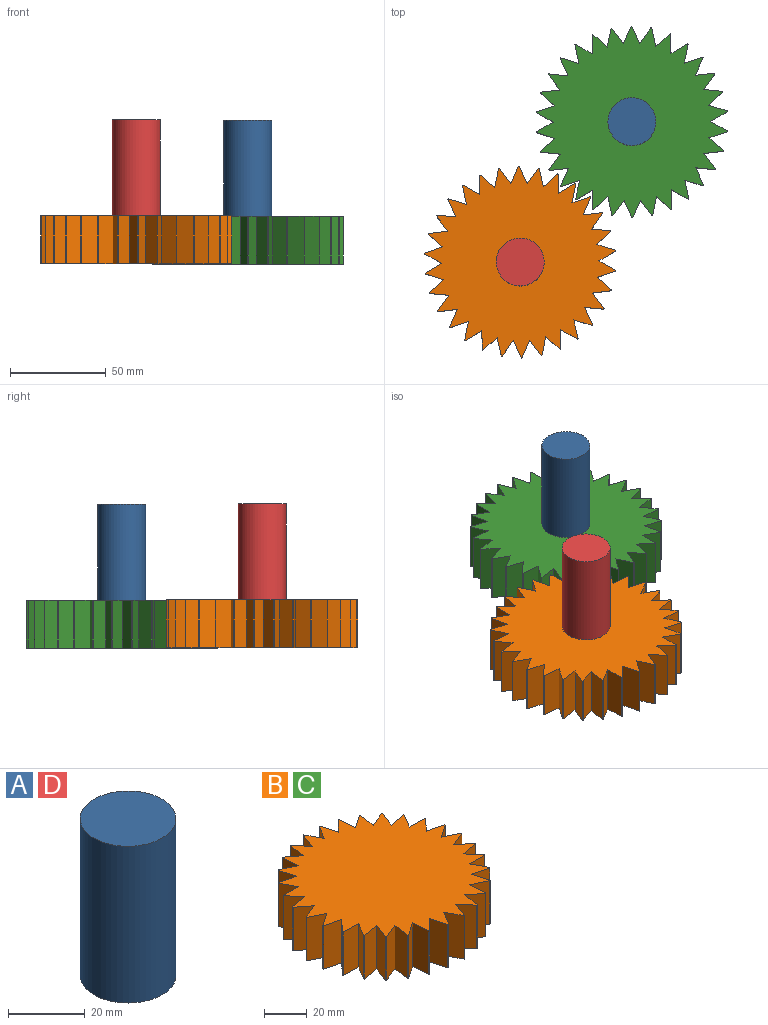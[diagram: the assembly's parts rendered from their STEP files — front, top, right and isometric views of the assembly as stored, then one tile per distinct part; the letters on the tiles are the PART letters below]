
ASSEMBLY  parts=4 mates=2
PART A: 3 faces, bbox 25x25x50 mm
  f0: cylinder r=12.5mm len=50mm, axis (0,0,-1), area 3927mm2, adj f1,f2
  f1: plane 25x25mm, normal (0,0,1), area 490.9mm2, adj f0
  f2: plane 25x25mm, normal (0,0,-1), area 490.9mm2, adj f0
PART B: 92 faces, bbox 100x99.8x25 mm
  f0: cylinder r=50mm len=25mm, axis (0,0,-1), area 11.4mm2, adj f30,f31,f59,f90
  f1: cylinder r=50mm len=25mm, axis (0,0,-1), area 11.4mm2, adj f30,f31,f77,f88
  f2: cylinder r=50mm len=25mm, axis (0,0,-1), area 11.4mm2, adj f30,f31,f55,f86
  f3: cylinder r=50mm len=25mm, axis (0,0,-1), area 11.4mm2, adj f30,f31,f49,f84
  f4: cylinder r=50mm len=25mm, axis (0,0,-1), area 11.4mm2, adj f30,f31,f82,f85
  f5: cylinder r=50mm len=25mm, axis (0,0,-1), area 11.4mm2, adj f30,f31,f63,f80
  f6: cylinder r=50mm len=25mm, axis (0,0,-1), area 11.4mm2, adj f30,f31,f33,f78
  f7: cylinder r=50mm len=25mm, axis (0,0,-1), area 11.4mm2, adj f30,f31,f71,f76
  f8: cylinder r=50mm len=25mm, axis (0,0,-1), area 11.4mm2, adj f30,f31,f69,f74
  f9: cylinder r=50mm len=25mm, axis (0,0,-1), area 11.4mm2, adj f30,f31,f39,f72
  f10: cylinder r=50mm len=25mm, axis (0,0,-1), area 11.4mm2, adj f30,f31,f67,f70
  f11: cylinder r=50mm len=25mm, axis (0,0,-1), area 11.4mm2, adj f30,f31,f68,f91
  f12: cylinder r=50mm len=25mm, axis (0,0,-1), area 11.4mm2, adj f30,f31,f66,f75
  f13: cylinder r=50mm len=25mm, axis (0,0,-1), area 11.4mm2, adj f30,f31,f53,f64
  f14: cylinder r=50mm len=25mm, axis (0,0,-1), area 11.4mm2, adj f30,f31,f62,f65
  f15: cylinder r=50mm len=25mm, axis (0,0,-1), area 11.4mm2, adj f30,f31,f60,f81
  f16: cylinder r=50mm len=25mm, axis (0,0,-1), area 11.4mm2, adj f30,f31,f58,f73
  f17: cylinder r=50mm len=25mm, axis (0,0,-1), area 11.4mm2, adj f30,f31,f56,f83
  f18: cylinder r=50mm len=25mm, axis (0,0,-1), area 11.4mm2, adj f30,f31,f47,f54
  f19: cylinder r=50mm len=25mm, axis (0,0,-1), area 11.4mm2, adj f30,f31,f35,f52
  f20: cylinder r=50mm len=25mm, axis (0,0,-1), area 11.4mm2, adj f30,f31,f50,f79
  f21: cylinder r=50mm len=25mm, axis (0,0,-1), area 11.4mm2, adj f30,f31,f48,f51
  f22: cylinder r=50mm len=25mm, axis (0,0,-1), area 11.4mm2, adj f30,f31,f46,f89
  f23: cylinder r=50mm len=25mm, axis (0,0,-1), area 11.4mm2, adj f30,f31,f37,f44
  f24: cylinder r=50mm len=25mm, axis (0,0,-1), area 11.4mm2, adj f30,f31,f42,f87
  f25: cylinder r=50mm len=25mm, axis (0,0,-1), area 11.4mm2, adj f30,f31,f40,f57
  f26: cylinder r=50mm len=25mm, axis (0,0,-1), area 11.4mm2, adj f30,f31,f38,f45
  f27: cylinder r=50mm len=25mm, axis (0,0,-1), area 11.4mm2, adj f30,f31,f36,f61
  f28: cylinder r=50mm len=25mm, axis (0,0,-1), area 11.4mm2, adj f30,f31,f34,f41
  f29: cylinder r=50mm len=25mm, axis (0,0,-1), area 11.4mm2, adj f30,f31,f32,f43
  f30: plane 99.96x99.77mm, normal (0,0,1), area 6504.8mm2, adj f0,f1,f2,f3,f4,f5,f6,f7
  f31: plane 99.96x99.77mm, normal (0,0,-1), area 6504.8mm2, adj f0,f1,f2,f3,f4,f5,f6,f7
  f32: plane 25x9mm, normal (0.44,0.9,0), area 250mm2, adj f29,f30,f31,f33
  f33: plane 25x9.97mm, normal (-1,-0.07,0), area 250mm2, adj f6,f30,f31,f32
  f34: plane 25x8.49mm, normal (0.85,-0.53,0), area 250mm2, adj f28,f30,f31,f35
  f35: plane 25x9.99mm, normal (0.03,1,0), area 250mm2, adj f19,f30,f31,f34
  f36: plane 25x9.71mm, normal (-0.24,-0.97,0), area 250mm2, adj f27,f30,f31,f37
  f37: plane 25x9.61mm, normal (0.96,0.28,0), area 250mm2, adj f23,f30,f31,f36
  f38: plane 25x7.89mm, normal (-0.61,-0.79,0), area 250mm2, adj f26,f30,f31,f39
  f39: plane 25x9.91mm, normal (0.99,-0.14,0), area 250mm2, adj f9,f30,f31,f38
  f40: plane 25x9.4mm, normal (0.94,-0.34,0), area 250mm2, adj f25,f30,f31,f41
  f41: plane 25x9.84mm, normal (-0.18,0.98,0), area 250mm2, adj f28,f30,f31,f40
  f42: plane 25x9.71mm, normal (0.24,0.97,0), area 250mm2, adj f24,f30,f31,f43
  f43: plane 25x9.61mm, normal (-0.96,-0.28,0), area 250mm2, adj f29,f30,f31,f42
  f44: plane 25x9mm, normal (-0.44,-0.9,0), area 250mm2, adj f23,f30,f31,f45
  f45: plane 25x9.97mm, normal (1,0.07,0), area 250mm2, adj f26,f30,f31,f44
  f46: plane 25x9.26mm, normal (-0.38,0.93,0), area 250mm2, adj f22,f30,f31,f47
  f47: plane 25x7.89mm, normal (-0.61,-0.79,0), area 250mm2, adj f18,f30,f31,f46
  f48: plane 25x8.82mm, normal (0.88,0.47,0), area 250mm2, adj f21,f30,f31,f49
  f49: plane 25x8.49mm, normal (-0.85,0.53,0), area 250mm2, adj f3,f30,f31,f48
  f50: plane 25x7.65mm, normal (0.76,0.64,0), area 250mm2, adj f20,f30,f31,f51
  f51: plane 25x9.4mm, normal (-0.94,0.34,0), area 250mm2, adj f21,f30,f31,f50
  f52: plane 25x7.21mm, normal (0.72,-0.69,0), area 250mm2, adj f19,f30,f31,f53
  f53: plane 25x9.71mm, normal (0.24,0.97,0), area 250mm2, adj f13,f30,f31,f52
  f54: plane 25x9.84mm, normal (-0.18,0.98,0), area 250mm2, adj f18,f30,f31,f55
  f55: plane 25x7.65mm, normal (-0.76,-0.64,0), area 250mm2, adj f2,f30,f31,f54
  f56: plane 25x9.91mm, normal (0.99,-0.14,0), area 250mm2, adj f17,f30,f31,f57
  f57: plane 25x9.26mm, normal (-0.38,0.93,0), area 250mm2, adj f25,f30,f31,f56
  f58: plane 25x8.82mm, normal (-0.88,-0.47,0), area 250mm2, adj f16,f30,f31,f59
  f59: plane 25x8.49mm, normal (0.85,-0.53,0), area 250mm2, adj f0,f30,f31,f58
  f60: plane 25x9.99mm, normal (-0.03,-1,0), area 250mm2, adj f15,f30,f31,f61
  f61: plane 25x8.82mm, normal (0.88,0.47,0), area 250mm2, adj f27,f30,f31,f60
  f62: plane 25x9.26mm, normal (0.38,-0.93,0), area 250mm2, adj f14,f30,f31,f63
  f63: plane 25x7.89mm, normal (0.61,0.79,0), area 250mm2, adj f5,f30,f31,f62
  f64: plane 25x8.28mm, normal (0.56,-0.83,0), area 250mm2, adj f13,f30,f31,f65
  f65: plane 25x9mm, normal (0.44,0.9,0), area 250mm2, adj f14,f30,f31,f64
  f66: plane 25x9.4mm, normal (-0.94,0.34,0), area 250mm2, adj f12,f30,f31,f67
  f67: plane 25x9.84mm, normal (0.18,-0.98,0), area 250mm2, adj f10,f30,f31,f66
  f68: plane 25x9.97mm, normal (-1,-0.07,0), area 250mm2, adj f11,f30,f31,f69
  f69: plane 25x8.28mm, normal (0.56,-0.83,0), area 250mm2, adj f8,f30,f31,f68
  f70: plane 25x8.49mm, normal (-0.85,0.53,0), area 250mm2, adj f10,f30,f31,f71
  f71: plane 25x9.99mm, normal (-0.03,-1,0), area 250mm2, adj f7,f30,f31,f70
  f72: plane 25x7.65mm, normal (-0.76,-0.64,0), area 250mm2, adj f9,f30,f31,f73
  f73: plane 25x9.4mm, normal (0.94,-0.34,0), area 250mm2, adj f16,f30,f31,f72
  f74: plane 25x9.91mm, normal (-0.99,0.14,0), area 250mm2, adj f8,f30,f31,f75
  f75: plane 25x9.26mm, normal (0.38,-0.93,0), area 250mm2, adj f12,f30,f31,f74
  f76: plane 25x7.21mm, normal (-0.72,0.69,0), area 250mm2, adj f7,f30,f31,f77
  f77: plane 25x9.71mm, normal (-0.24,-0.97,0), area 250mm2, adj f1,f30,f31,f76
  f78: plane 25x7.89mm, normal (0.61,0.79,0), area 250mm2, adj f6,f30,f31,f79
  f79: plane 25x9.91mm, normal (-0.99,0.14,0), area 250mm2, adj f20,f30,f31,f78
  f80: plane 25x9.84mm, normal (0.18,-0.98,0), area 250mm2, adj f5,f30,f31,f81
  f81: plane 25x7.65mm, normal (0.76,0.64,0), area 250mm2, adj f15,f30,f31,f80
  f82: plane 25x9.97mm, normal (1,0.07,0), area 250mm2, adj f4,f30,f31,f83
  f83: plane 25x8.28mm, normal (-0.56,0.83,0), area 250mm2, adj f17,f30,f31,f82
  f84: plane 25x9.61mm, normal (0.96,0.28,0), area 250mm2, adj f3,f30,f31,f85
  f85: plane 25x7.21mm, normal (-0.72,0.69,0), area 250mm2, adj f4,f30,f31,f84
  f86: plane 25x9.99mm, normal (0.03,1,0), area 250mm2, adj f2,f30,f31,f87
  f87: plane 25x8.82mm, normal (-0.88,-0.47,0), area 250mm2, adj f24,f30,f31,f86
  f88: plane 25x8.28mm, normal (-0.56,0.83,0), area 250mm2, adj f1,f30,f31,f89
  f89: plane 25x9mm, normal (-0.44,-0.9,0), area 250mm2, adj f22,f30,f31,f88
  f90: plane 25x9.61mm, normal (-0.96,-0.28,0), area 250mm2, adj f0,f30,f31,f91
  f91: plane 25x7.21mm, normal (0.72,-0.69,0), area 250mm2, adj f11,f30,f31,f90
PART C: same geometry as B
PART D: same geometry as A
PLACE A rot(axis=(0.94,0.35,0),180deg) t=(3.18,-43.79,117.51)mm fixed
PLACE B rot(axis=(0,0,1),8.7deg) t=(-145.61,-100.16,55.35)mm
PLACE C rot(axis=(0,0,-1),123.9deg) t=(-87.33,-26.92,55.01)mm
PLACE D rot(axis=(-0.55,-0.84,0),180deg) t=(-102.87,-18.62,117.85)mm fixed
MATE revolute A.f0 <-> C.f0  axis (0,0,-1) through (-87.33,-26.92,67.51)mm
MATE revolute D.f0 <-> B.f0  axis (0,0,-1) through (-145.61,-100.16,67.85)mm
